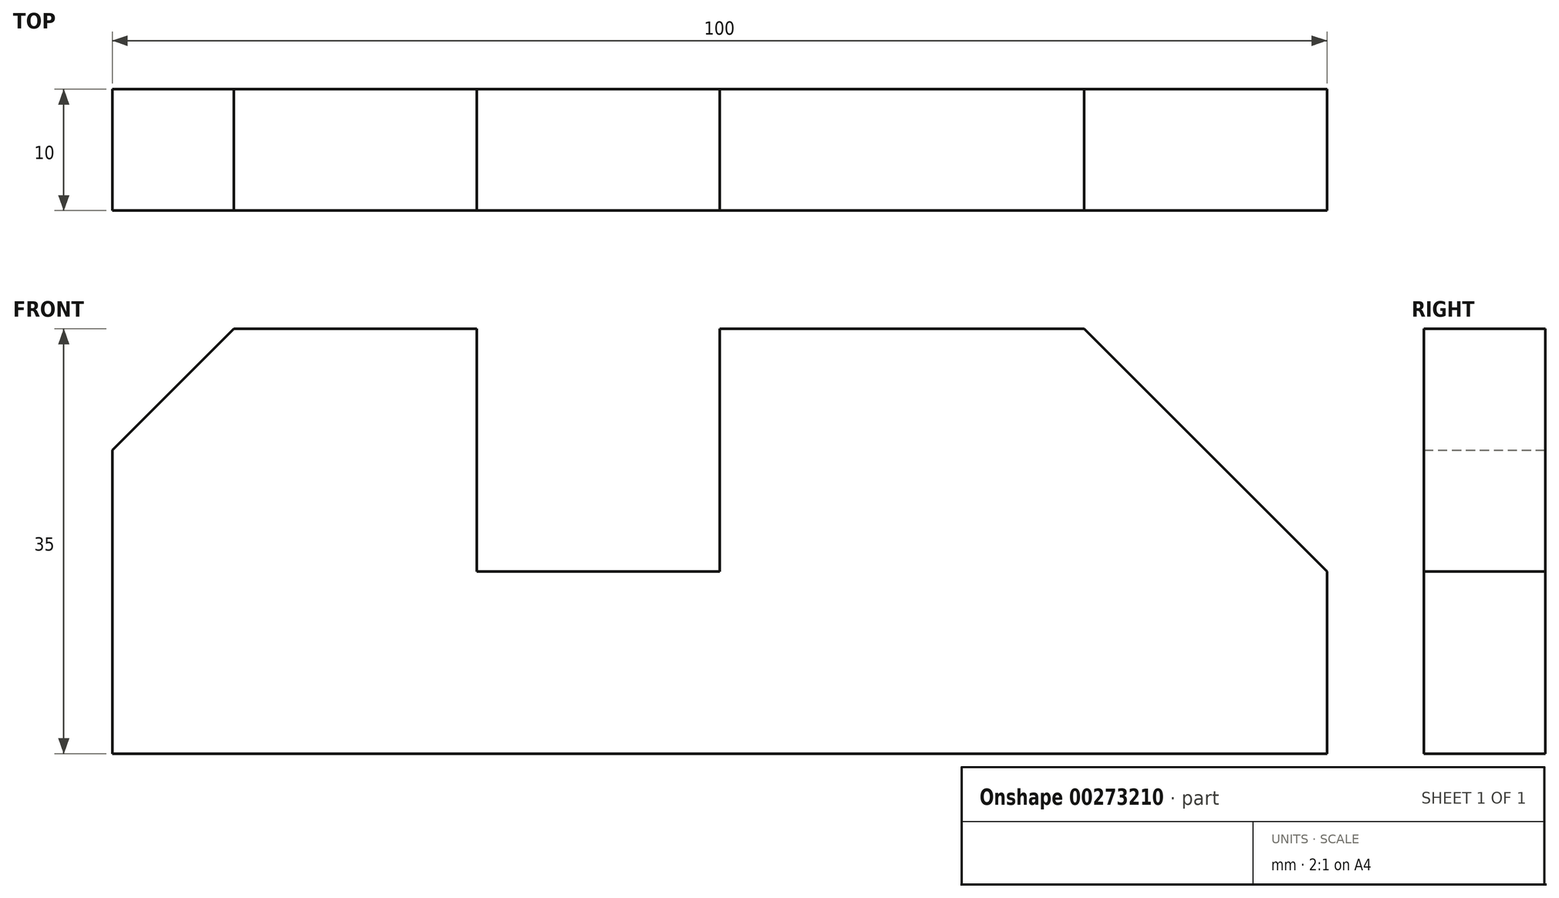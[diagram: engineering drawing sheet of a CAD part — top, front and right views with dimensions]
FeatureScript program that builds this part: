
annotation { "Feature Type Name" : "Feature", "Feature Type Description" : "" }
export const myFeature = defineFeature(function(context is Context, id is Id, definition is map)
    precondition{}
    {
        {
            var Q0;
            Q0=qCreatedBy(makeId("Front.planeOp"),FACE);
            var sketch = newSketch(context, id + "F0", { "sketchPlane" : qUnion([Q0])});
            skLineSegment(sketch, "E0", {"start": v(0, 0) * mm, "end": v(100, 0) * mm});
            skLineSegment(sketch, "E1", {"start": v(100, 0) * mm, "end": v(100, 15) * mm});
            skLineSegment(sketch, "E2", {"start": v(100, 15) * mm, "end": v(80, 35) * mm});
            skLineSegment(sketch, "E3", {"start": v(80, 35) * mm, "end": v(50, 35) * mm});
            skLineSegment(sketch, "E4", {"start": v(50, 35) * mm, "end": v(50, 15) * mm});
            skLineSegment(sketch, "E5", {"start": v(50, 15) * mm, "end": v(30, 15) * mm});
            skLineSegment(sketch, "E6", {"start": v(30, 15) * mm, "end": v(30, 35) * mm});
            skLineSegment(sketch, "E7", {"start": v(30, 35) * mm, "end": v(10, 35) * mm});
            skLineSegment(sketch, "E8", {"start": v(0, 25) * mm, "end": v(10, 35) * mm});
            skLineSegment(sketch, "E9", {"start": v(0, 25) * mm, "end": v(0, 0) * mm});
            skSolve(sketch);
        }
        {
            var Q0;
            Q0 = qSketchRegion(id + "F0", true);
            extrude(context, id + "F1", {"entities" : qUnion([Q0]), "depth" : 10 * mm});
        }
    });
